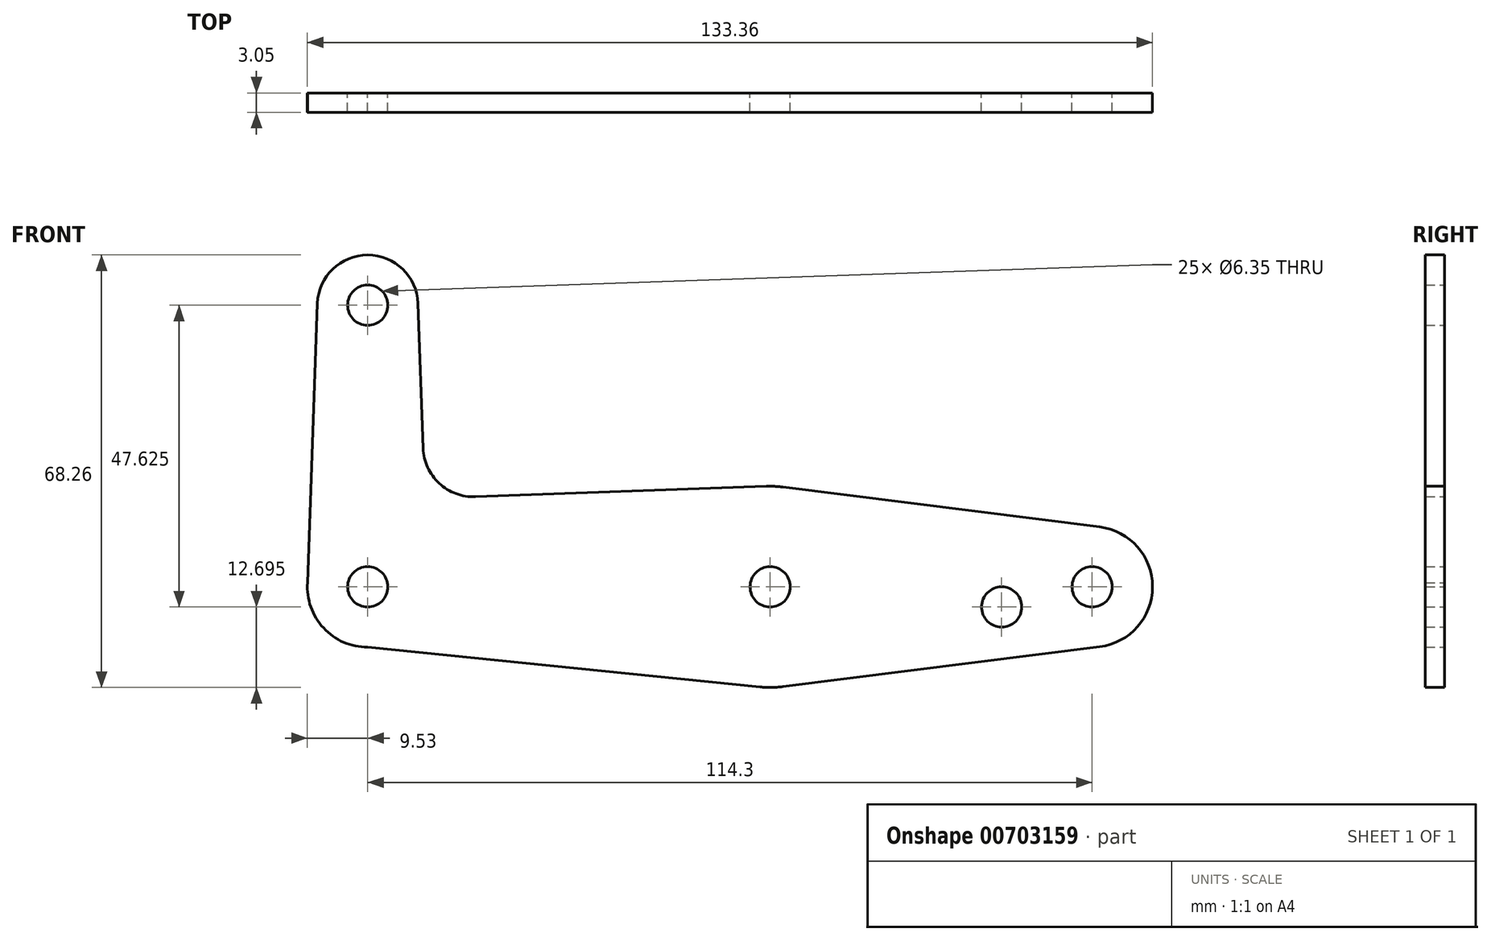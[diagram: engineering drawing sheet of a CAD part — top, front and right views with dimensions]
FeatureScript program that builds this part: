
annotation { "Feature Type Name" : "Feature", "Feature Type Description" : "" }
export const myFeature = defineFeature(function(context is Context, id is Id, definition is map)
    precondition{}
    {
        {
            var Q0;
            Q0=qCreatedBy(makeId("Front.planeOp"),FACE);
            var sketch = newSketch(context, id + "F0", { "sketchPlane" : qUnion([Q0])});
            skLineSegment(sketch, "E0", {"start": v(0, 0) * mm, "end": v(0, 44.45) * mm});
            skLineSegment(sketch, "E1", {"start": v(0, 44.45) * mm, "end": v(0, 0) * mm, "construction": true});
            skLineSegment(sketch, "E2", {"start": v(0, 0) * mm, "end": v(114.3, 0) * mm, "construction": true});
            skCircle(sketch, "E3", {"center": v(114.3, 0) * mm, "radius": 9.53 * mm});
            skCircle(sketch, "E4", {"center": v(0, 44.45) * mm, "radius": 7.94 * mm});
            skCircle(sketch, "E5", {"center": v(0, 0) * mm, "radius": 9.53 * mm});
            skLineSegment(sketch, "E6", {"start": v(-9.53, 0) * mm, "end": v(-7.93, 44.73) * mm});
            skCircle(sketch, "E7", {"center": v(0, 0) * mm, "radius": 3.18 * mm});
            skCircle(sketch, "E8", {"center": v(0, 44.45) * mm, "radius": 3.18 * mm});
            skCircle(sketch, "E9", {"center": v(63.5, 0) * mm, "radius": 3.18 * mm});
            skCircle(sketch, "E10", {"center": v(114.3, 0) * mm, "radius": 3.18 * mm});
            skLineSegment(sketch, "E11", {"start": v(8.75, 21.88) * mm, "end": v(7.93, 44.73) * mm});
            skCircle(sketch, "E12", {"center": v(63.5, 0) * mm, "radius": 15.88 * mm});
            skLineSegment(sketch, "E13", {"start": v(65.48, -15.75) * mm, "end": v(115.5, -9.45) * mm});
            skLineSegment(sketch, "E14", {"start": v(65.48, 15.75) * mm, "end": v(115.5, 9.45) * mm});
            skLineSegment(sketch, "E15", {"start": v(16.98, 14.22) * mm, "end": v(62.93, 15.86) * mm});
            skLineSegment(sketch, "E16", {"start": v(0, -9.53) * mm, "end": v(61.9, -15.8) * mm});
            skPoint(sketch, "E17.newPointB", {"position": v(0, 13.62) * mm});
            skArc(sketch, "E17.filletArc", {"start": v(8.75, 21.88) * mm, "mid": v(11.28, 16.35) * mm, "end": v(16.98, 14.22) * mm});
            skCircle(sketch, "E18", {"center": v(100.03, -3.18) * mm, "radius": 3.18 * mm});
            skSolve(sketch);
        }
        {
            var Q0;
            Q0 = qSketchRegion(id + "F0", true);
            extrude(context, id + "F1", {"entities" : qUnion([Q0]), "depth" : 3.05 * mm, "offsetDistance" : 25.4 * mm});
        }
    });
